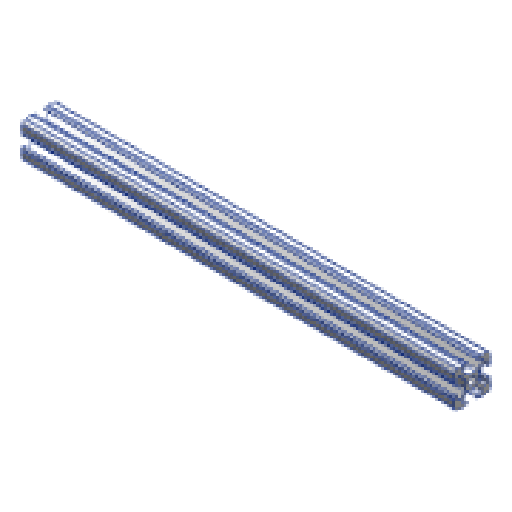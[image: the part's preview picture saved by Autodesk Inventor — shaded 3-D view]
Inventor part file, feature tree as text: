
AUTODESK INVENTOR PART (.ipt)
format: ipt  version: 2025 (Build 290162000, 162)  size: 246,272 bytes
history: native  units: in
note: dims shown in document units (in); Inventor stores cm internally (conversion verified against a paired STEP export)
features: extrude x1, sketch x1
ambient origin geometry x8: Origin, YZ Plane, XZ Plane, XY Plane, X Axis, Y Axis, Z Axis, Center Point
bodies: Solid1 (feature_tree)
feature tree (2):
  extrude  "Extrusion1"  [1 undecoded]
  sketch  "Sketch1"  dims[d0=12.0in d1=0.0in]
note: 1 required parameter value undecoded (feature->parameter linkage not recoverable at this tier; creation-order binding heuristic only, values carry confidence <= 0.55)
